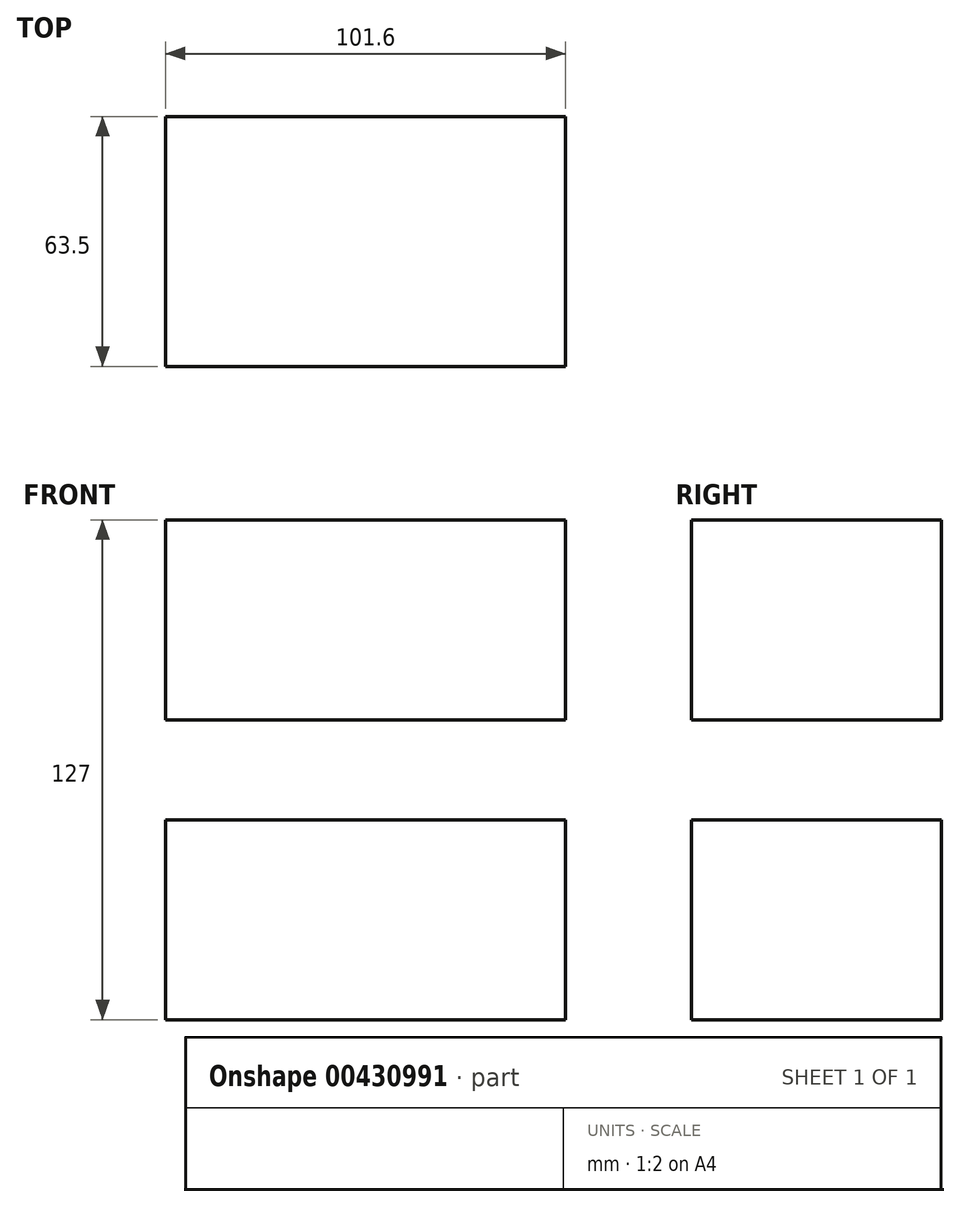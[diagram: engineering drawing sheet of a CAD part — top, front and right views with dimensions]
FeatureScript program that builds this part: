
annotation { "Feature Type Name" : "Feature", "Feature Type Description" : "" }
export const myFeature = defineFeature(function(context is Context, id is Id, definition is map)
    precondition{}
    {
        {
            var Q0;
            Q0=qCreatedBy(makeId("Front.planeOp"),FACE);
            var sketch = newSketch(context, id + "F0", { "sketchPlane" : qUnion([Q0])});
            skLineSegment(sketch, "E0.bottom", {"start": v(-108.05, 31.79) * mm, "end": v(-6.45, 31.79) * mm});
            skLineSegment(sketch, "E0.top", {"start": v(-108.05, -19.01) * mm, "end": v(-6.45, -19.01) * mm});
            skLineSegment(sketch, "E0.left", {"start": v(-108.05, 31.79) * mm, "end": v(-108.05, -19.01) * mm});
            skLineSegment(sketch, "E0.right", {"start": v(-6.45, 31.79) * mm, "end": v(-6.45, -19.01) * mm});
            skLineSegment(sketch, "E1.bottom", {"start": v(-108.05, 107.99) * mm, "end": v(-6.45, 107.99) * mm});
            skLineSegment(sketch, "E1.top", {"start": v(-108.05, 57.19) * mm, "end": v(-6.45, 57.19) * mm});
            skLineSegment(sketch, "E1.left", {"start": v(-108.05, 107.99) * mm, "end": v(-108.05, 57.19) * mm});
            skLineSegment(sketch, "E1.right", {"start": v(-6.45, 107.99) * mm, "end": v(-6.45, 57.19) * mm});
            skPoint(sketch, "E2.firstSnap0", {"position": v(-57.25, 107.99) * mm});
            skLineSegment(sketch, "E2.bottom", {"start": v(-57.25, 151.73) * mm, "end": v(0, 151.73) * mm});
            skLineSegment(sketch, "E2.top", {"start": v(-57.25, 197.7) * mm, "end": v(0, 197.7) * mm});
            skLineSegment(sketch, "E2.left", {"start": v(-57.25, 151.73) * mm, "end": v(-57.25, 197.7) * mm});
            skLineSegment(sketch, "E2.right", {"start": v(0, 151.73) * mm, "end": v(0, 197.7) * mm});
            skLineSegment(sketch, "E3", {"start": v(-108.05, 31.79) * mm, "end": v(-108.05, 57.19) * mm});
            skLineSegment(sketch, "E4", {"start": v(-6.45, 31.79) * mm, "end": v(-6.45, 57.19) * mm});
            skSolve(sketch);
        }
        {
            var Q0;
            Q0=makeQuery(id+"F0.imprint","IMPRINT",FACE,{"disambiguationData":[TD([[makeQuery(id+"F0.imprint","IMPRINT",EDGE,{"derivedFrom":sQuery(id+"F0.wireOp",EDGE,"E1.bottom")}),-1.0]])]});
            var Q1;
            Q1=makeQuery(id+"F0.imprint","IMPRINT",FACE,{"disambiguationData":[TD([[makeQuery(id+"F0.imprint","IMPRINT",EDGE,{"derivedFrom":sQuery(id+"F0.wireOp",EDGE,"E0.bottom")}),-1.0]])]});
            extrude(context, id + "F1", {"entities" : qUnion([Q0, Q1]), "depth" : 63.5 * mm});
        }
    });
